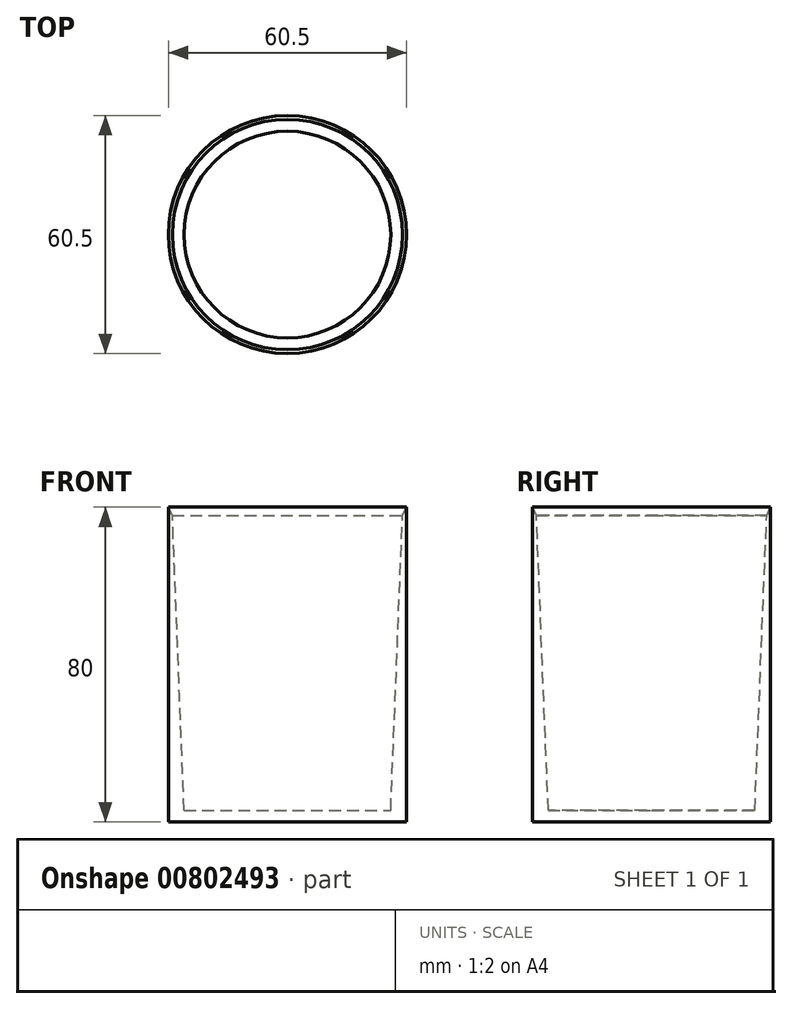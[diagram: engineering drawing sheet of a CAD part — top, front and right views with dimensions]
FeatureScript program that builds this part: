
annotation { "Feature Type Name" : "Feature", "Feature Type Description" : "" }
export const myFeature = defineFeature(function(context is Context, id is Id, definition is map)
    precondition{}
    {
        {
            var Q0;
            Q0=qCreatedBy(makeId("Right.planeOp"),FACE);
            var sketch = newSketch(context, id + "F0", { "sketchPlane" : qUnion([Q0])});
            skLineSegment(sketch, "E0", {"start": v(-30.25, 80) * mm, "end": v(-30.25, 0) * mm});
            skLineSegment(sketch, "E1", {"start": v(-30.25, 0) * mm, "end": v(0, 0) * mm});
            skLineSegment(sketch, "E2", {"start": v(0, 0) * mm, "end": v(0, 3) * mm});
            skLineSegment(sketch, "E3", {"start": v(0, 3) * mm, "end": v(-26.25, 3) * mm});
            skLineSegment(sketch, "E4", {"start": v(-30.25, 80) * mm, "end": v(-29.25, 77.94) * mm});
            skLineSegment(sketch, "E5", {"start": v(-29.25, 77.94) * mm, "end": v(-26.25, 3) * mm});
            skSolve(sketch);
        }
        {
            var Q0;
            Q0=makeQuery(id+"F0.imprint","IMPRINT",FACE,{"disambiguationData":[TD([[makeQuery(id+"F0.imprint","IMPRINT",EDGE,{"derivedFrom":sQuery(id+"F0.wireOp",EDGE,"E0")}),1.0]])]});
            var Q1;
            Q1=sQuery(id+"F0.wireOp",EDGE,"E2");
            revolve(context, id + "F1", {"surfaceOperationType" : NewSurfaceOperationType.NEW, "entities" : qUnion([Q0]), "axis" : qUnion([Q1]), "revolveType" : RevolveType.FULL});
        }
        {
            var Q0;
            Q0=makeQuery(id+"F1.opRevolve","SWEPT_BODY",BODY,{"disambiguationData":[OSD([sQuery(id+"F0.wireOp",EDGE,"E0"),sQuery(id+"F0.wireOp",EDGE,"E1"),sQuery(id+"F0.wireOp",EDGE,"E2"),sQuery(id+"F0.wireOp",EDGE,"E3"),sQuery(id+"F0.wireOp",EDGE,"E4"),sQuery(id+"F0.wireOp",EDGE,"E5")])]});
            transform(context, id + "F2", {"entities" : qUnion([Q0]), "transformType" : TransformType.TRANSLATION_3D, "dx" : 0 * mm, "dy" : -62 * mm, "dz" : -6.94E-15 * mm, "makeCopy" : true});
        }
        {
            var Q0;
            Q0=makeQuery(id+"F2.opPattern","COPY",BODY,{"derivedFrom":makeQuery(id+"F1.opRevolve","SWEPT_BODY",BODY,{"disambiguationData":[OSD([sQuery(id+"F0.wireOp",EDGE,"E0"),sQuery(id+"F0.wireOp",EDGE,"E1"),sQuery(id+"F0.wireOp",EDGE,"E2"),sQuery(id+"F0.wireOp",EDGE,"E3"),sQuery(id+"F0.wireOp",EDGE,"E4"),sQuery(id+"F0.wireOp",EDGE,"E5")])]}),"instanceName":"1"});
            deleteBodies(context, id + "F3", {"entities" : qUnion([Q0])});
        }
        {
            var Q0;
            Q0=makeQuery(id+"F0.imprint","IMPRINT",FACE,{"disambiguationData":[TD([[makeQuery(id+"F0.imprint","IMPRINT",EDGE,{"derivedFrom":sQuery(id+"F0.wireOp",EDGE,"E0")}),1.0]])]});
            var Q1;
            Q1=sQuery(id+"F0.wireOp",EDGE,"E2");
            revolve(context, id + "F4", {"surfaceOperationType" : NewSurfaceOperationType.NEW, "entities" : qUnion([Q0]), "axis" : qUnion([Q1]), "revolveType" : RevolveType.FULL});
        }
    });
